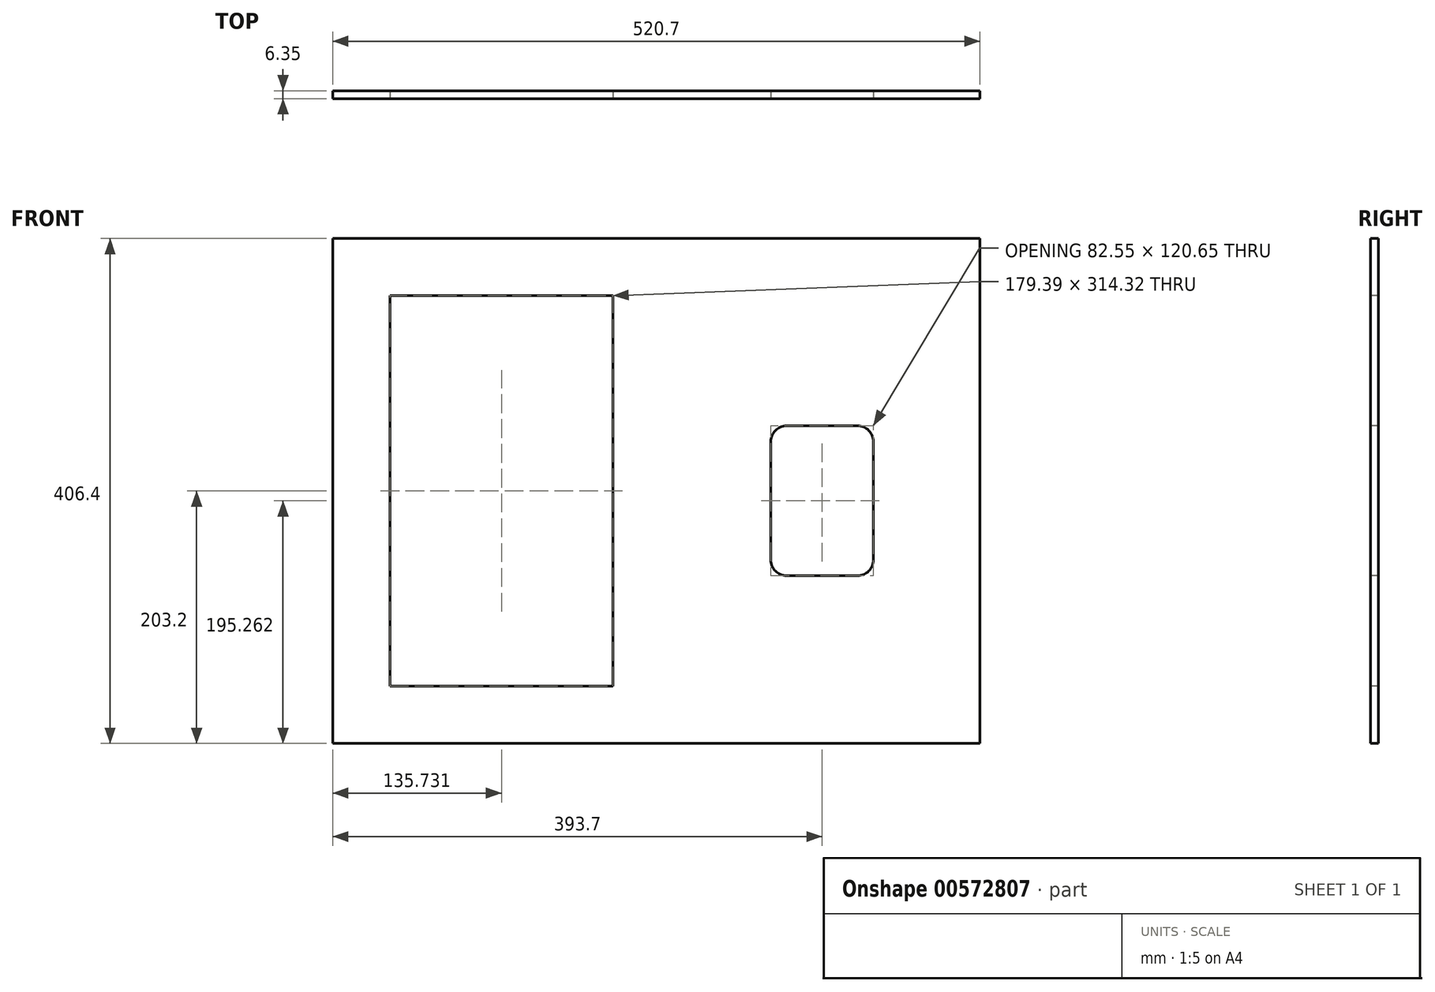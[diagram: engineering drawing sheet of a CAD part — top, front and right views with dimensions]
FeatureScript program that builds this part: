
annotation { "Feature Type Name" : "Feature", "Feature Type Description" : "" }
export const myFeature = defineFeature(function(context is Context, id is Id, definition is map)
    precondition{}
    {
        {
            var Q0;
            Q0=qCreatedBy(makeId("Front.planeOp"),FACE);
            var sketch = newSketch(context, id + "F0", { "sketchPlane" : qUnion([Q0])});
            skLineSegment(sketch, "E0.bottom", {"start": v(-260.35, 203.2) * mm, "end": v(260.35, 203.2) * mm});
            skLineSegment(sketch, "E0.top", {"start": v(-260.35, -203.2) * mm, "end": v(260.35, -203.2) * mm});
            skLineSegment(sketch, "E0.left", {"start": v(-260.35, 203.2) * mm, "end": v(-260.35, -203.2) * mm});
            skLineSegment(sketch, "E0.right", {"start": v(260.35, 203.2) * mm, "end": v(260.35, -203.2) * mm});
            skLineSegment(sketch, "E1", {"start": v(0, 203.2) * mm, "end": v(0, -203.2) * mm, "construction": true});
            skLineSegment(sketch, "E2.bottom", {"start": v(-214.31, 157.16) * mm, "end": v(-34.93, 157.16) * mm});
            skLineSegment(sketch, "E2.top", {"start": v(-214.31, -157.16) * mm, "end": v(-34.92, -157.16) * mm});
            skLineSegment(sketch, "E2.left", {"start": v(-214.31, 157.16) * mm, "end": v(-214.31, -157.16) * mm});
            skLineSegment(sketch, "E2.right", {"start": v(-34.93, 157.16) * mm, "end": v(-34.92, -157.16) * mm});
            skLineSegment(sketch, "E3", {"start": v(-260.35, 0) * mm, "end": v(260.35, 0) * mm, "construction": true});
            skLineSegment(sketch, "E4.bottom", {"start": v(104.78, 52.39) * mm, "end": v(161.93, 52.39) * mm});
            skLineSegment(sketch, "E4.top", {"start": v(104.78, -68.26) * mm, "end": v(161.93, -68.26) * mm});
            skLineSegment(sketch, "E4.left", {"start": v(92.08, 39.69) * mm, "end": v(92.08, -55.56) * mm});
            skLineSegment(sketch, "E4.right", {"start": v(174.63, 39.69) * mm, "end": v(174.63, -55.56) * mm});
            skPoint(sketch, "E5.visualSharp", {"position": v(92.08, 52.39) * mm});
            skArc(sketch, "E5.filletArc", {"start": v(104.78, 52.39) * mm, "mid": v(95.8, 48.67) * mm, "end": v(92.08, 39.69) * mm});
            skPoint(sketch, "E6.visualSharp", {"position": v(92.08, -68.26) * mm});
            skArc(sketch, "E6.filletArc", {"start": v(92.08, -55.56) * mm, "mid": v(95.8, -64.54) * mm, "end": v(104.78, -68.26) * mm});
            skPoint(sketch, "E7.visualSharp", {"position": v(174.63, -68.26) * mm});
            skArc(sketch, "E7.filletArc", {"start": v(161.93, -68.26) * mm, "mid": v(170.9, -64.54) * mm, "end": v(174.62, -55.56) * mm});
            skPoint(sketch, "E8.visualSharp", {"position": v(174.63, 52.39) * mm});
            skArc(sketch, "E8.filletArc", {"start": v(174.63, 39.69) * mm, "mid": v(170.9, 48.67) * mm, "end": v(161.93, 52.39) * mm});
            skSolve(sketch);
        }
        {
            var Q0;
            Q0=makeQuery(id+"F0.imprint","IMPRINT",FACE,{"disambiguationData":[TD([[makeQuery(id+"F0.imprint","IMPRINT",EDGE,{"derivedFrom":sQuery(id+"F0.wireOp",EDGE,"E0.bottom")}),-1.0]])]});
            extrude(context, id + "F1", {"entities" : qUnion([Q0]), "oppositeDirection" : true, "depth" : 6.35 * mm, "offsetDistance" : 25.4 * mm});
        }
    });
